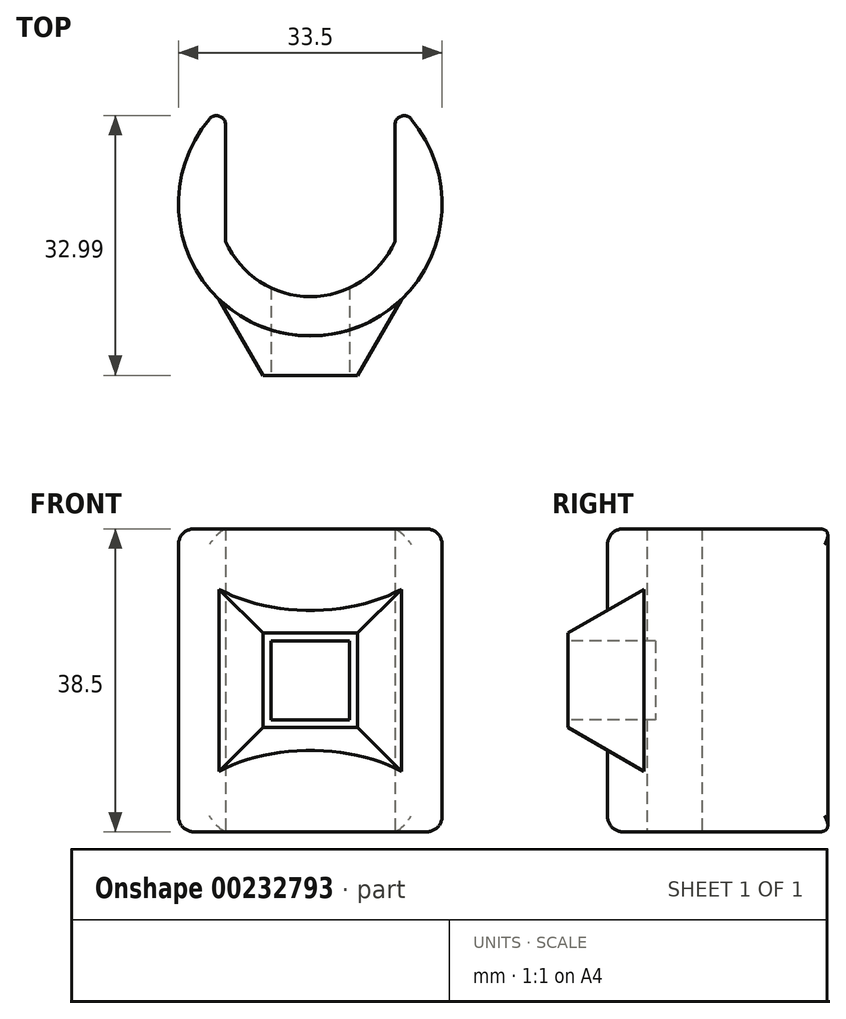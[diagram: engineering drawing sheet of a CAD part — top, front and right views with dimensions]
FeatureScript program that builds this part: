
annotation { "Feature Type Name" : "Feature", "Feature Type Description" : "" }
export const myFeature = defineFeature(function(context is Context, id is Id, definition is map)
    precondition{}
    {
        {
            var Q0;
            Q0=qCreatedBy(makeId("Top.planeOp"),FACE);
            var sketch = newSketch(context, id + "F0", { "sketchPlane" : qUnion([Q0])});
            skArc(sketch, "E0", {"start": v(-10.75, -4.74) * mm, "mid": v(0, -11.75) * mm, "end": v(10.75, -4.74) * mm});
            skArc(sketch, "E1", {"start": v(-10.75, 12.85) * mm, "mid": v(0, -16.75) * mm, "end": v(10.75, 12.85) * mm});
            skLineSegment(sketch, "E2.left", {"start": v(-10.75, 12.85) * mm, "end": v(-10.75, -4.74) * mm});
            skLineSegment(sketch, "E2.right", {"start": v(10.75, 12.85) * mm, "end": v(10.75, -4.74) * mm});
            skSolve(sketch);
        }
        {
            var Q0;
            Q0=qSketchRegion(id+"F0",true);
            extrude(context, id + "F1", {"entities" : qUnion([Q0]), "depth" : 38.5 * mm, "offsetDistance" : 25 * mm});
        }
        {
            var Q0;
            Q0=qCreatedBy(makeId("Front.planeOp"),FACE);
            var Q1;
            Q1 = qBodyType(qCreatedBy(id + "F3" ,EDGE), BodyType.WIRE);
            cPlane(context, id + "F2", {"entities" : qUnion([Q0, Q1]), "cplaneType" : CPlaneType.OFFSET, "offset" : 21.75 * mm, "width" : 150 * mm, "height" : 150 * mm});
        }
        {
            var Q0;
            Q0=qCreatedBy(id+"F2.planeOp",FACE);
            var sketch = newSketch(context, id + "F3", { "sketchPlane" : qUnion([Q0])});
            skLineSegment(sketch, "E3.bottom", {"start": v(-6, 25.25) * mm, "end": v(6, 25.25) * mm});
            skLineSegment(sketch, "E3.top", {"start": v(-6, 13.25) * mm, "end": v(6, 13.25) * mm});
            skLineSegment(sketch, "E3.left", {"start": v(-6, 25.25) * mm, "end": v(-6, 13.25) * mm});
            skLineSegment(sketch, "E3.right", {"start": v(6, 25.25) * mm, "end": v(6, 13.25) * mm});
            skPoint(sketch, "E3.middle", {"position": v(0, 19.25) * mm});
            skSolve(sketch);
        }
        {
            var Q0;
            Q0=qSketchRegion(id+"F3",true);
            extrude(context, id + "F4", {"entities" : qUnion([Q0]), "operationType" : NewBodyOperationType.ADD, "oppositeDirection" : true, "depth" : 10 * mm, "hasDraft" : true, "draftAngle" : 30 * degree, "hasSecondDirectionDraft" : true, "secondDirectionDraftAngle" : 55 * degree, "offsetDistance" : 25 * mm});
        }
        {
            var Q0;
            Q0=makeQuery(id+"F4.opExtrude","CAP_FACE",FACE,{"disambiguationData":[OSD([sQuery(id+"F3.wireOp",EDGE,"E3.bottom"),sQuery(id+"F3.wireOp",EDGE,"E3.top"),sQuery(id+"F3.wireOp",EDGE,"E3.left"),sQuery(id+"F3.wireOp",EDGE,"E3.right")])],"isStart":true});
            var sketch = newSketch(context, id + "F5", { "sketchPlane" : qUnion([Q0])});
            skLineSegment(sketch, "E4", {"start": v(-6, 19.25) * mm, "end": v(6, 19.25) * mm, "construction": true});
            skLineSegment(sketch, "E5", {"start": v(-11.56, 30.8) * mm, "end": v(-11.56, 7.7) * mm, "construction": true});
            skLineSegment(sketch, "E6.bottom", {"start": v(-5, 24.25) * mm, "end": v(5, 24.25) * mm});
            skLineSegment(sketch, "E6.top", {"start": v(-5, 14.25) * mm, "end": v(5, 14.25) * mm});
            skLineSegment(sketch, "E6.left", {"start": v(-5, 24.25) * mm, "end": v(-5, 14.25) * mm});
            skLineSegment(sketch, "E6.right", {"start": v(5, 24.25) * mm, "end": v(5, 14.25) * mm});
            skPoint(sketch, "E6.middle", {"position": v(0, 19.25) * mm});
            skSolve(sketch);
        }
        {
            var Q0;
            Q0 = qSketchRegion(id + "F5", true);
            extrude(context, id + "F6", {"entities" : qUnion([Q0]), "operationType" : NewBodyOperationType.REMOVE, "endBound" : BoundingType.THROUGH_ALL, "oppositeDirection" : true, "depth" : 10 * mm, "offsetDistance" : 25 * mm});
        }
        {
            var Q0;
            Q0=makeQuery(id+"F1.opExtrude","CAP_EDGE",EDGE,{"disambiguationData":[OSD([sQuery(id+"F0.wireOp",EDGE,"E1")])],"isStart":true});
            var Q1;
            Q1=makeQuery(id+"F1.opExtrude","CAP_EDGE",EDGE,{"disambiguationData":[OSD([sQuery(id+"F0.wireOp",EDGE,"E1")])],"isStart":false});
            fillet(context, id + "F7", {"entities" : qUnion([Q0, Q1]), "radius" : 2 * mm, "tangentPropagation" : true, "allowEdgeOverflow" : false});
        }
        {
            var Q0;
            Q0=makeQuery(id+"F1.opExtrude","SWEPT_EDGE",EDGE,{"disambiguationData":[OSD([sQuery(id+"F0.wireOp",EDGE,"E1"),sQuery(id+"F0.wireOp",EDGE,"E2.right")])]});
            var Q1;
            Q1=makeQuery(id+"F1.opExtrude","SWEPT_EDGE",EDGE,{"disambiguationData":[OSD([sQuery(id+"F0.wireOp",EDGE,"E1"),sQuery(id+"F0.wireOp",EDGE,"E2.left")])]});
            fillet(context, id + "F8", {"entities" : qUnion([Q0, Q1]), "radius" : 1.15 * mm, "allowEdgeOverflow" : false});
        }
    });
